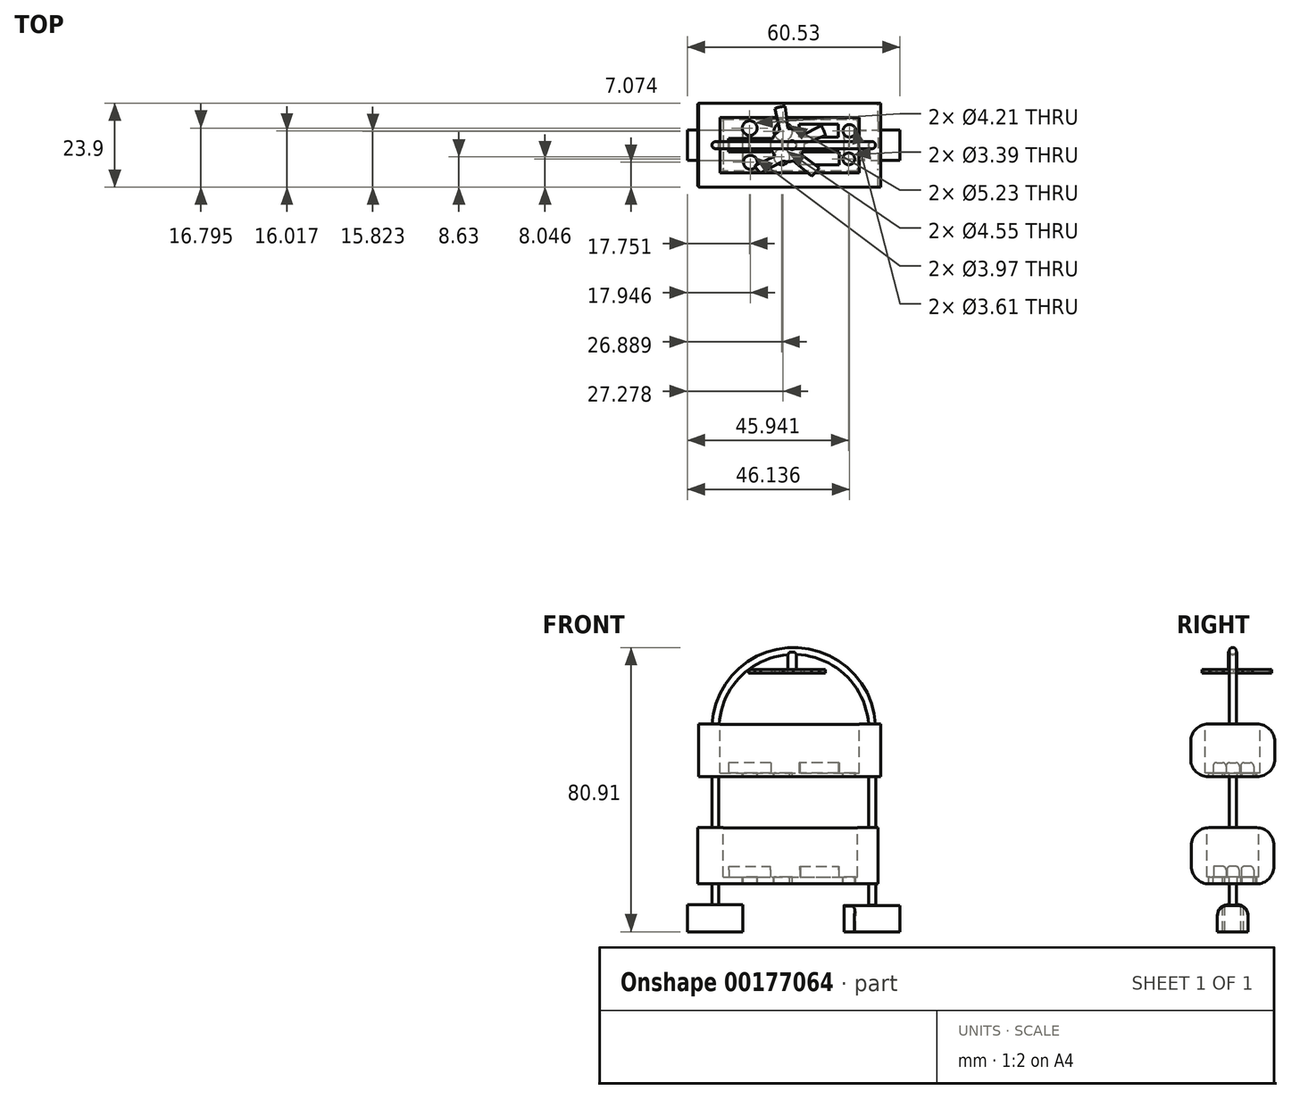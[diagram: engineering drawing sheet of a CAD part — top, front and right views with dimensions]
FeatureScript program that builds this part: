
annotation { "Feature Type Name" : "Feature", "Feature Type Description" : "" }
export const myFeature = defineFeature(function(context is Context, id is Id, definition is map)
    precondition{}
    {
        {
            var Q0;
            Q0=qCreatedBy(makeId("Front.planeOp"),FACE);
            var sketch = newSketch(context, id + "F0", { "sketchPlane" : qUnion([Q0])});
            skLineSegment(sketch, "E0", {"start": v(-49.97, -24.03) * mm, "end": v(-49.97, 25.97) * mm});
            skLineSegment(sketch, "E1", {"start": v(-5.33, -24.03) * mm, "end": v(-5.33, 25.97) * mm});
            skArc(sketch, "E2", {"start": v(-5.33, 25.97) * mm, "mid": v(-27.65, 48.3) * mm, "end": v(-49.97, 25.97) * mm});
            skSolve(sketch);
        }
        {
            var Q0;
            Q0=qCreatedBy(makeId("Top.planeOp"),FACE);
            var Q1;
            Q1=sQuery(id+"F0.wireOp",VERTEX,"E0.start");
            cPlane(context, id + "F1", {"entities" : qUnion([Q0, Q1]), "cplaneType" : CPlaneType.PLANE_POINT, "offset" : 25 * mm, "width" : 150 * mm, "height" : 150 * mm});
        }
        {
            var Q0;
            Q0=qCreatedBy(id+"F1.planeOp",FACE);
            var sketch = newSketch(context, id + "F2", { "sketchPlane" : qUnion([Q0])});
            skCircle(sketch, "E3", {"center": v(-44.5, -28.72) * mm, "radius": 0.47 * mm});
            skCircle(sketch, "E4", {"center": v(-43.63, -30.22) * mm, "radius": 0.12 * mm});
            skCircle(sketch, "E5", {"center": v(-44.5, -28.7) * mm, "radius": 5 * mm});
            skCircle(sketch, "E6", {"center": v(-44.47, -28.8) * mm, "radius": 1.1 * mm});
            skCircle(sketch, "E7", {"center": v(-49.97, 0) * mm, "radius": 1 * mm});
            skCircle(sketch, "E8", {"center": v(-5.33, 0) * mm, "radius": 1 * mm});
            skSolve(sketch);
        }
        {
            var Q0;
            Q0=makeQuery(id+"F2.imprint","IMPRINT",FACE,{"disambiguationData":[TD([[makeQuery(id+"F2.imprint","IMPRINT",EDGE,{"derivedFrom":sQuery(id+"F2.wireOp",EDGE,"E7")}),1.0]])]});
            var Q1;
            Q1=sQuery(id+"F0.wireOp",EDGE,"E0");
            var Q2;
            Q2=sQuery(id+"F0.wireOp",EDGE,"E2");
            var Q3;
            Q3=sQuery(id+"F0.wireOp",EDGE,"E1");
            sweep(context, id + "F3", {"profiles" : qUnion([Q0]), "path" : qUnion([Q1, Q2, Q3])});
        }
        {
            var Q0;
            Q0=qCreatedBy(makeId("Front.planeOp"),FACE);
            var sketch = newSketch(context, id + "F4", { "sketchPlane" : qUnion([Q0])});
            skLineSegment(sketch, "E9.bottom", {"start": v(-57.95, -23.93) * mm, "end": v(-42.2, -23.93) * mm});
            skLineSegment(sketch, "E9.top", {"start": v(-57.95, -31.62) * mm, "end": v(-42.2, -31.62) * mm});
            skLineSegment(sketch, "E9.left", {"start": v(-57.95, -23.93) * mm, "end": v(-57.95, -31.62) * mm});
            skLineSegment(sketch, "E9.right", {"start": v(-42.2, -23.93) * mm, "end": v(-42.2, -31.62) * mm});
            skLineSegment(sketch, "E10.bottom", {"start": v(-13.35, -24.12) * mm, "end": v(2.58, -24.12) * mm});
            skLineSegment(sketch, "E10.top", {"start": v(-13.35, -31.62) * mm, "end": v(2.58, -31.62) * mm});
            skLineSegment(sketch, "E10.left", {"start": v(-13.35, -24.12) * mm, "end": v(-13.35, -31.62) * mm});
            skLineSegment(sketch, "E10.right", {"start": v(2.58, -24.12) * mm, "end": v(2.58, -31.62) * mm});
            skSolve(sketch);
        }
        {
            var Q0;
            Q0 = qSketchRegion(id + "F4", true);
            extrude(context, id + "F5", {"entities" : qUnion([Q0]), "operationType" : NewBodyOperationType.ADD, "endBound" : BoundingType.SYMMETRIC, "depth" : 8.7 * mm});
        }
        {
            var Q0;
            Q0=qCreatedBy(makeId("Top.planeOp"),FACE);
            cPlane(context, id + "F6", {"entities" : qUnion([Q0]), "cplaneType" : CPlaneType.OFFSET, "offset" : 20 * mm, "width" : 150 * mm, "height" : 150 * mm});
        }
        {
            var Q0;
            Q0=qCreatedBy(id+"F6.planeOp",FACE);
            var sketch = newSketch(context, id + "F7", { "sketchPlane" : qUnion([Q0])});
            skLineSegment(sketch, "E11.bottom", {"start": v(-54.79, 11.95) * mm, "end": v(-2.88, 11.95) * mm});
            skLineSegment(sketch, "E11.top", {"start": v(-54.79, -11.95) * mm, "end": v(-2.88, -11.95) * mm});
            skLineSegment(sketch, "E11.left", {"start": v(-54.79, 11.95) * mm, "end": v(-54.79, -11.95) * mm});
            skLineSegment(sketch, "E11.right", {"start": v(-2.88, 11.95) * mm, "end": v(-2.88, -11.95) * mm});
            skPoint(sketch, "E11.middle", {"position": v(-28.84, 0) * mm});
            skSolve(sketch);
        }
        {
            var Q0;
            Q0 = qSketchRegion(id + "F7", true);
            extrude(context, id + "F8", {"entities" : qUnion([Q0]), "operationType" : NewBodyOperationType.ADD, "endBound" : BoundingType.SYMMETRIC, "depth" : 15 * mm});
        }
        {
            var Q0;
            Q0=makeQuery(id+"F8.opExtrude","CAP_FACE",FACE,{"disambiguationData":[OSD([sQuery(id+"F7.wireOp",EDGE,"E11.bottom"),sQuery(id+"F7.wireOp",EDGE,"E11.top"),sQuery(id+"F7.wireOp",EDGE,"E11.left"),sQuery(id+"F7.wireOp",EDGE,"E11.right")])],"isStart":false});
            var sketch = newSketch(context, id + "F9", { "sketchPlane" : qUnion([Q0])});
            skLineSegment(sketch, "E12.bottom", {"start": v(-48.6, 7.83) * mm, "end": v(-9.06, 7.83) * mm});
            skLineSegment(sketch, "E12.top", {"start": v(-48.6, -7.83) * mm, "end": v(-9.06, -7.83) * mm});
            skLineSegment(sketch, "E12.left", {"start": v(-48.6, 7.83) * mm, "end": v(-48.6, -7.83) * mm});
            skLineSegment(sketch, "E12.right", {"start": v(-9.06, 7.83) * mm, "end": v(-9.06, -7.83) * mm});
            skPoint(sketch, "E12.middle", {"position": v(-28.84, 0) * mm});
            skPoint(sketch, "E12.middle.positionSnap0", {"position": v(-28.84, 11.95) * mm});
            skPoint(sketch, "E12.middle.positionSnap1", {"position": v(-2.88, 0) * mm});
            skPoint(sketch, "E12.centerSnap0", {"position": v(-28.84, 11.95) * mm});
            skPoint(sketch, "E12.centerSnap1", {"position": v(-2.88, 0) * mm});
            skSolve(sketch);
        }
        {
            var Q0;
            Q0 = qSketchRegion(id + "F9", true);
            extrude(context, id + "F10", {"entities" : qUnion([Q0]), "operationType" : NewBodyOperationType.REMOVE, "oppositeDirection" : true, "depth" : 14 * mm});
        }
        {
            var Q0;
            Q0=qCreatedBy(makeId("Top.planeOp"),FACE);
            cPlane(context, id + "F11", {"entities" : qUnion([Q0]), "cplaneType" : CPlaneType.OFFSET, "offset" : 10 * mm, "oppositeDirection" : true, "width" : 150 * mm, "height" : 150 * mm});
        }
        {
            var Q0;
            Q0=qCreatedBy(id+"F11.planeOp",FACE);
            var sketch = newSketch(context, id + "F12", { "sketchPlane" : qUnion([Q0])});
            skLineSegment(sketch, "E13.bottom", {"start": v(-55.05, 11.74) * mm, "end": v(-3.67, 11.74) * mm});
            skLineSegment(sketch, "E13.top", {"start": v(-55.05, -11.74) * mm, "end": v(-3.67, -11.74) * mm});
            skLineSegment(sketch, "E13.left", {"start": v(-55.05, 11.74) * mm, "end": v(-55.05, -11.74) * mm});
            skLineSegment(sketch, "E13.right", {"start": v(-3.67, 11.74) * mm, "end": v(-3.67, -11.74) * mm});
            skPoint(sketch, "E13.middle", {"position": v(-29.36, 0) * mm});
            skSolve(sketch);
        }
        {
            var Q0;
            Q0 = qSketchRegion(id + "F12", true);
            extrude(context, id + "F13", {"entities" : qUnion([Q0]), "operationType" : NewBodyOperationType.ADD, "endBound" : BoundingType.SYMMETRIC, "depth" : 16 * mm});
        }
        {
            var Q0;
            Q0=makeQuery(id+"F13.opExtrude","CAP_FACE",FACE,{"disambiguationData":[OSD([sQuery(id+"F12.wireOp",EDGE,"E13.bottom"),sQuery(id+"F12.wireOp",EDGE,"E13.top"),sQuery(id+"F12.wireOp",EDGE,"E13.left"),sQuery(id+"F12.wireOp",EDGE,"E13.right")])],"isStart":false});
            var sketch = newSketch(context, id + "F14", { "sketchPlane" : qUnion([Q0])});
            skLineSegment(sketch, "E14.bottom", {"start": v(-47.71, 7.34) * mm, "end": v(-9.54, 7.34) * mm});
            skLineSegment(sketch, "E14.top", {"start": v(-47.71, -7.34) * mm, "end": v(-9.54, -7.34) * mm});
            skLineSegment(sketch, "E14.left", {"start": v(-47.71, 7.34) * mm, "end": v(-47.71, -7.34) * mm});
            skLineSegment(sketch, "E14.right", {"start": v(-9.54, 7.34) * mm, "end": v(-9.54, -7.34) * mm});
            skPoint(sketch, "E14.middle", {"position": v(-28.63, 0) * mm});
            skSolve(sketch);
        }
        {
            var Q0;
            Q0=makeQuery(id+"F14.imprint","IMPRINT",FACE,{"disambiguationData":[TD([[makeQuery(id+"F14.imprint","IMPRINT",EDGE,{"derivedFrom":sQuery(id+"F14.wireOp",EDGE,"E14.bottom")}),-1.0]])]});
            extrude(context, id + "F15", {"entities" : qUnion([Q0]), "operationType" : NewBodyOperationType.REMOVE, "oppositeDirection" : true, "depth" : 14 * mm});
        }
        {
            var Q0;
            Q0=makeQuery(id+"F10.boolean.opBoolean","COPY",FACE,{"derivedFrom":makeQuery(id+"F10.opExtrude","CAP_FACE",FACE,{"disambiguationData":[OSD([sQuery(id+"F9.wireOp",EDGE,"E12.bottom"),sQuery(id+"F9.wireOp",EDGE,"E12.top"),sQuery(id+"F9.wireOp",EDGE,"E12.left"),sQuery(id+"F9.wireOp",EDGE,"E12.right")])],"isStart":false})});
            var sketch = newSketch(context, id + "F16", { "sketchPlane" : qUnion([Q0])});
            skLineSegment(sketch, "E15.bottom", {"start": v(-34.2, -1.9) * mm, "end": v(-46.23, -1.9) * mm});
            skLineSegment(sketch, "E15.top", {"start": v(-34.2, 1.9) * mm, "end": v(-46.23, 1.9) * mm});
            skLineSegment(sketch, "E15.left", {"start": v(-34.2, -1.9) * mm, "end": v(-34.2, 1.9) * mm});
            skLineSegment(sketch, "E15.right", {"start": v(-46.23, -1.9) * mm, "end": v(-46.23, 1.9) * mm});
            skPoint(sketch, "E15.middle", {"position": v(-40.22, 0) * mm});
            skLineSegment(sketch, "E16.bottom", {"start": v(-15.01, 2.26) * mm, "end": v(-26.11, 2.26) * mm});
            skLineSegment(sketch, "E16.top", {"start": v(-15.01, 5.96) * mm, "end": v(-26.11, 5.96) * mm});
            skLineSegment(sketch, "E16.left", {"start": v(-15.01, 2.26) * mm, "end": v(-15.01, 5.96) * mm});
            skLineSegment(sketch, "E16.right", {"start": v(-26.11, 2.26) * mm, "end": v(-26.11, 5.96) * mm});
            skPoint(sketch, "E16.middle", {"position": v(-20.56, 4.11) * mm});
            skLineSegment(sketch, "E17.bottom", {"start": v(-14.78, -5.6) * mm, "end": v(-25.88, -5.6) * mm});
            skLineSegment(sketch, "E17.top", {"start": v(-14.78, -1.9) * mm, "end": v(-25.88, -1.9) * mm});
            skLineSegment(sketch, "E17.left", {"start": v(-14.78, -5.6) * mm, "end": v(-14.78, -1.9) * mm});
            skLineSegment(sketch, "E17.right", {"start": v(-25.88, -5.6) * mm, "end": v(-25.88, -1.9) * mm});
            skPoint(sketch, "E17.middle", {"position": v(-20.33, -3.75) * mm});
            skSolve(sketch);
        }
        {
            var Q0;
            Q0 = qSketchRegion(id + "F16", true);
            extrude(context, id + "F17", {"entities" : qUnion([Q0]), "operationType" : NewBodyOperationType.ADD, "depth" : 3 * mm});
        }
        {
            var Q0;
            Q0=makeQuery(id+"F17.opExtrude","CAP_EDGE",EDGE,{"disambiguationData":[OSD([sQuery(id+"F16.wireOp",EDGE,"E15.bottom")])],"isStart":false});
            var Q1;
            Q1=makeQuery(id+"F17.opExtrude","CAP_EDGE",EDGE,{"disambiguationData":[OSD([sQuery(id+"F16.wireOp",EDGE,"E17.bottom")])],"isStart":false});
            var Q2;
            Q2=makeQuery(id+"F17.opExtrude","CAP_EDGE",EDGE,{"disambiguationData":[OSD([sQuery(id+"F16.wireOp",EDGE,"E15.top")])],"isStart":false});
            var Q3;
            Q3=makeQuery(id+"F17.opExtrude","CAP_EDGE",EDGE,{"disambiguationData":[OSD([sQuery(id+"F16.wireOp",EDGE,"E16.bottom")])],"isStart":false});
            var Q4;
            Q4=makeQuery(id+"F17.opExtrude","CAP_EDGE",EDGE,{"disambiguationData":[OSD([sQuery(id+"F16.wireOp",EDGE,"E17.top")])],"isStart":false});
            var Q5;
            Q5=makeQuery(id+"F17.opExtrude","CAP_EDGE",EDGE,{"disambiguationData":[OSD([sQuery(id+"F16.wireOp",EDGE,"E16.top")])],"isStart":false});
            fillet(context, id + "F18", {"entities" : qUnion([Q0, Q1, Q2, Q3, Q4, Q5]), "radius" : 1 * mm, "tangentPropagation" : true, "allowEdgeOverflow" : false});
        }
        {
            var Q0;
            Q0=makeQuery(id+"F10.boolean.opBoolean","COPY",FACE,{"derivedFrom":makeQuery(id+"F10.opExtrude","CAP_FACE",FACE,{"disambiguationData":[OSD([sQuery(id+"F9.wireOp",EDGE,"E12.bottom"),sQuery(id+"F9.wireOp",EDGE,"E12.top"),sQuery(id+"F9.wireOp",EDGE,"E12.left"),sQuery(id+"F9.wireOp",EDGE,"E12.right")])],"isStart":false})});
            var sketch = newSketch(context, id + "F19", { "sketchPlane" : qUnion([Q0])});
            skCircle(sketch, "E18", {"center": v(-40.2, 4.84) * mm, "radius": 2.1 * mm});
            skCircle(sketch, "E19", {"center": v(-30.67, 3.87) * mm, "radius": 2.62 * mm});
            skCircle(sketch, "E20", {"center": v(-31.06, -3.32) * mm, "radius": 2.28 * mm});
            skCircle(sketch, "E21", {"center": v(-40, -4.88) * mm, "radius": 1.98 * mm});
            skCircle(sketch, "E22", {"center": v(-11.81, 4.07) * mm, "radius": 1.8 * mm});
            skCircle(sketch, "E23", {"center": v(-12, -3.9) * mm, "radius": 1.7 * mm});
            skSolve(sketch);
        }
        {
            var Q0;
            Q0 = qSketchRegion(id + "F19", true);
            extrude(context, id + "F20", {"entities" : qUnion([Q0]), "operationType" : NewBodyOperationType.REMOVE, "endBound" : BoundingType.THROUGH_ALL, "oppositeDirection" : true, "depth" : 25 * mm});
        }
        {
            var Q0;
            Q0=makeQuery(id+"F15.boolean.opBoolean","COPY",FACE,{"derivedFrom":makeQuery(id+"F15.opExtrude","CAP_FACE",FACE,{"disambiguationData":[OSD([sQuery(id+"F14.wireOp",EDGE,"E14.bottom"),sQuery(id+"F14.wireOp",EDGE,"E14.top"),sQuery(id+"F14.wireOp",EDGE,"E14.left"),sQuery(id+"F14.wireOp",EDGE,"E14.right")])],"isStart":false})});
            var sketch = newSketch(context, id + "F21", { "sketchPlane" : qUnion([Q0])});
            skLineSegment(sketch, "E24.bottom", {"start": v(-46.05, 1.81) * mm, "end": v(-34.26, 1.81) * mm});
            skLineSegment(sketch, "E24.top", {"start": v(-46.05, -1.65) * mm, "end": v(-34.26, -1.65) * mm});
            skLineSegment(sketch, "E24.left", {"start": v(-46.05, 1.81) * mm, "end": v(-46.05, -1.65) * mm});
            skLineSegment(sketch, "E24.right", {"start": v(-34.26, 1.81) * mm, "end": v(-34.26, -1.65) * mm});
            skLineSegment(sketch, "E25.bottom", {"start": v(-25.94, 5.97) * mm, "end": v(-14.84, 5.97) * mm});
            skLineSegment(sketch, "E25.top", {"start": v(-25.94, 2.4) * mm, "end": v(-14.84, 2.4) * mm});
            skLineSegment(sketch, "E25.left", {"start": v(-25.94, 5.97) * mm, "end": v(-25.94, 2.4) * mm});
            skLineSegment(sketch, "E25.right", {"start": v(-14.84, 5.97) * mm, "end": v(-14.84, 2.4) * mm});
            skLineSegment(sketch, "E26.bottom", {"start": v(-25.82, -1.89) * mm, "end": v(-14.84, -1.89) * mm});
            skLineSegment(sketch, "E26.top", {"start": v(-25.82, -5.47) * mm, "end": v(-14.84, -5.47) * mm});
            skLineSegment(sketch, "E26.left", {"start": v(-25.82, -1.89) * mm, "end": v(-25.82, -5.47) * mm});
            skLineSegment(sketch, "E26.right", {"start": v(-14.84, -1.89) * mm, "end": v(-14.84, -5.47) * mm});
            skSolve(sketch);
        }
        {
            var Q0;
            Q0 = qSketchRegion(id + "F21", true);
            extrude(context, id + "F22", {"entities" : qUnion([Q0]), "operationType" : NewBodyOperationType.ADD, "depth" : 3 * mm});
        }
        {
            var Q0;
            Q0=makeQuery(id+"F22.opExtrude","CAP_EDGE",EDGE,{"disambiguationData":[OSD([sQuery(id+"F21.wireOp",EDGE,"E25.top")])],"isStart":false});
            var Q1;
            Q1=makeQuery(id+"F22.opExtrude","CAP_EDGE",EDGE,{"disambiguationData":[OSD([sQuery(id+"F21.wireOp",EDGE,"E25.bottom")])],"isStart":false});
            var Q2;
            Q2=makeQuery(id+"F22.opExtrude","CAP_EDGE",EDGE,{"disambiguationData":[OSD([sQuery(id+"F21.wireOp",EDGE,"E24.top")])],"isStart":false});
            var Q3;
            Q3=makeQuery(id+"F22.opExtrude","CAP_EDGE",EDGE,{"disambiguationData":[OSD([sQuery(id+"F21.wireOp",EDGE,"E26.bottom")])],"isStart":true});
            var Q4;
            Q4=makeQuery(id+"F22.opExtrude","CAP_EDGE",EDGE,{"disambiguationData":[OSD([sQuery(id+"F21.wireOp",EDGE,"E26.bottom")])],"isStart":false});
            var Q5;
            Q5=makeQuery(id+"F22.opExtrude","CAP_EDGE",EDGE,{"disambiguationData":[OSD([sQuery(id+"F21.wireOp",EDGE,"E24.bottom")])],"isStart":false});
            fillet(context, id + "F23", {"entities" : qUnion([Q0, Q1, Q2, Q3, Q4, Q5]), "radius" : 1 * mm, "tangentPropagation" : true, "allowEdgeOverflow" : false});
        }
        {
            var Q0;
            Q0=makeQuery(id+"F8.opExtrude","CAP_EDGE",EDGE,{"disambiguationData":[OSD([sQuery(id+"F7.wireOp",EDGE,"E11.top")])],"isStart":false});
            var Q1;
            Q1=makeQuery(id+"F8.opExtrude","CAP_EDGE",EDGE,{"disambiguationData":[OSD([sQuery(id+"F7.wireOp",EDGE,"E11.bottom")])],"isStart":false});
            var Q2;
            Q2=makeQuery(id+"F13.opExtrude","CAP_EDGE",EDGE,{"disambiguationData":[OSD([sQuery(id+"F12.wireOp",EDGE,"E13.top")])],"isStart":false});
            var Q3;
            Q3=makeQuery(id+"F13.opExtrude","CAP_EDGE",EDGE,{"disambiguationData":[OSD([sQuery(id+"F12.wireOp",EDGE,"E13.bottom")])],"isStart":false});
            fillet(context, id + "F24", {"entities" : qUnion([Q0, Q1, Q2, Q3]), "radius" : 5 * mm, "tangentPropagation" : true, "allowEdgeOverflow" : false});
        }
        {
            var Q0;
            Q0=makeQuery(id+"F8.opExtrude","CAP_EDGE",EDGE,{"disambiguationData":[OSD([sQuery(id+"F7.wireOp",EDGE,"E11.top")])],"isStart":true});
            var Q1;
            Q1=makeQuery(id+"F8.opExtrude","CAP_EDGE",EDGE,{"disambiguationData":[OSD([sQuery(id+"F7.wireOp",EDGE,"E11.bottom")])],"isStart":true});
            var Q2;
            Q2=makeQuery(id+"F13.opExtrude","CAP_EDGE",EDGE,{"disambiguationData":[OSD([sQuery(id+"F12.wireOp",EDGE,"E13.bottom")])],"isStart":true});
            var Q3;
            Q3=makeQuery(id+"F13.opExtrude","CAP_EDGE",EDGE,{"disambiguationData":[OSD([sQuery(id+"F12.wireOp",EDGE,"E13.top")])],"isStart":true});
            fillet(context, id + "F25", {"entities" : qUnion([Q0, Q1, Q2, Q3]), "radius" : 5 * mm, "tangentPropagation" : true, "allowEdgeOverflow" : false});
        }
        {
            var Q0;
            Q0=makeQuery(id+"F5.opExtrude","CAP_EDGE",EDGE,{"disambiguationData":[OSD([sQuery(id+"F4.wireOp",EDGE,"E9.bottom")])],"isStart":false});
            var Q1;
            Q1=makeQuery(id+"F5.opExtrude","CAP_EDGE",EDGE,{"disambiguationData":[OSD([sQuery(id+"F4.wireOp",EDGE,"E9.bottom")])],"isStart":true});
            var Q2;
            Q2=makeQuery(id+"F5.opExtrude","CAP_EDGE",EDGE,{"disambiguationData":[OSD([sQuery(id+"F4.wireOp",EDGE,"E10.bottom")])],"isStart":false});
            var Q3;
            Q3=makeQuery(id+"F5.opExtrude","CAP_EDGE",EDGE,{"disambiguationData":[OSD([sQuery(id+"F4.wireOp",EDGE,"E10.bottom")])],"isStart":true});
            fillet(context, id + "F26", {"entities" : qUnion([Q0, Q1, Q2, Q3]), "radius" : 3 * mm, "tangentPropagation" : true, "allowEdgeOverflow" : false});
        }
        {
            var Q0;
            Q0=qCreatedBy(id+"F6.planeOp",FACE);
            cPlane(context, id + "F27", {"entities" : qUnion([Q0]), "cplaneType" : CPlaneType.OFFSET, "offset" : 28 * mm, "width" : 150 * mm, "height" : 150 * mm});
        }
        {
            var Q0;
            Q0=qCreatedBy(id+"F27.planeOp",FACE);
            var sketch = newSketch(context, id + "F28", { "sketchPlane" : qUnion([Q0])});
            skCircle(sketch, "E27", {"center": v(-28.14, 0) * mm, "radius": 1.24 * mm});
            skSolve(sketch);
        }
        {
            var Q0;
            Q0 = qSketchRegion(id + "F28", true);
            extrude(context, id + "F29", {"entities" : qUnion([Q0]), "operationType" : NewBodyOperationType.ADD, "oppositeDirection" : true, "depth" : 5 * mm});
        }
        {
            var Q0;
            Q0=makeQuery(id+"F29.opExtrude","CAP_FACE",FACE,{"disambiguationData":[OSD([sQuery(id+"F28.wireOp",EDGE,"E27")])],"isStart":false});
            var sketch = newSketch(context, id + "F30", { "sketchPlane" : qUnion([Q0])});
            skCircle(sketch, "E28", {"center": v(-29.38, 0) * mm, "radius": 11.08 * mm});
            skSolve(sketch);
        }
        {
            var Q0;
            Q0 = qSketchRegion(id + "F30", true);
            extrude(context, id + "F31", {"entities" : qUnion([Q0]), "operationType" : NewBodyOperationType.ADD, "depth" : 1 * mm});
        }
        {
            var Q0;
            Q0=makeQuery(id+"F31.opExtrude","CAP_FACE",FACE,{"disambiguationData":[OSD([sQuery(id+"F30.wireOp",EDGE,"E28")])],"isStart":true});
            var sketch = newSketch(context, id + "F32", { "sketchPlane" : qUnion([Q0])});
            skCircle(sketch, "E29", {"center": v(-29.38, 0) * mm, "radius": 4.71 * mm});
            skLineSegment(sketch, "E30", {"start": v(-25.53, 2.72) * mm, "end": v(-19.82, 5.61) * mm});
            skLineSegment(sketch, "E31", {"start": v(-24.73, 0.3) * mm, "end": v(-18.66, 2.8) * mm});
            skLineSegment(sketch, "E32", {"start": v(-25.49, -2.66) * mm, "end": v(-20.43, -6.53) * mm});
            skLineSegment(sketch, "E33", {"start": v(-27.77, -4.43) * mm, "end": v(-22.54, -8.72) * mm});
            skLineSegment(sketch, "E34", {"start": v(-32.95, -3.07) * mm, "end": v(-38.78, -5.87) * mm});
            skLineSegment(sketch, "E35", {"start": v(-30.7, -4.52) * mm, "end": v(-37.1, -7.94) * mm});
            skLineSegment(sketch, "E36", {"start": v(-33.75, 1.76) * mm, "end": v(-40.32, 1.76) * mm});
            skLineSegment(sketch, "E37", {"start": v(-40.4, -1.1) * mm, "end": v(-33.75, -1.1) * mm});
            skLineSegment(sketch, "E38", {"start": v(-33.75, -1.1) * mm, "end": v(-34.1, -1) * mm});
            skLineSegment(sketch, "E39", {"start": v(-31.59, 4.16) * mm, "end": v(-33.07, 10.44) * mm});
            skLineSegment(sketch, "E40", {"start": v(-29.33, 4.71) * mm, "end": v(-30.05, 11.06) * mm});
            skSolve(sketch);
        }
        {
            var Q0;
            {var subQ0=sQuery(id+"F32.wireOp",EDGE,"E30");Q0=makeQuery(id+"F32.imprint","IMPRINT",FACE,{"disambiguationData":[TD([[makeQuery(id+"F32.imprint","IMPRINT",EDGE,{"derivedFrom":subQ0}),1.0]])]});}
            var Q1;
            {var subQ0=sQuery(id+"F32.wireOp",EDGE,"E32");Q1=makeQuery(id+"F32.imprint","IMPRINT",FACE,{"disambiguationData":[TD([[makeQuery(id+"F32.imprint","IMPRINT",EDGE,{"derivedFrom":subQ0}),1.0]])]});}
            var Q2;
            {var subQ0=sQuery(id+"F32.wireOp",EDGE,"E33");Q2=makeQuery(id+"F32.imprint","IMPRINT",FACE,{"disambiguationData":[TD([[makeQuery(id+"F32.imprint","IMPRINT",EDGE,{"derivedFrom":subQ0}),-1.0]])]});}
            var Q3;
            {var subQ0=sQuery(id+"F32.wireOp",EDGE,"E36");Q3=makeQuery(id+"F32.imprint","IMPRINT",FACE,{"disambiguationData":[TD([[makeQuery(id+"F32.imprint","IMPRINT",EDGE,{"derivedFrom":subQ0}),-1.0]])]});}
            var Q4;
            {var subQ0=sQuery(id+"F32.wireOp",EDGE,"E34");Q4=makeQuery(id+"F32.imprint","IMPRINT",FACE,{"disambiguationData":[TD([[makeQuery(id+"F32.imprint","IMPRINT",EDGE,{"derivedFrom":subQ0}),-1.0]])]});}
            extrude(context, id + "F33", {"entities" : qUnion([Q0, Q1, Q2, Q3, Q4]), "operationType" : NewBodyOperationType.REMOVE, "oppositeDirection" : true, "depth" : 9 * mm});
        }
    });
